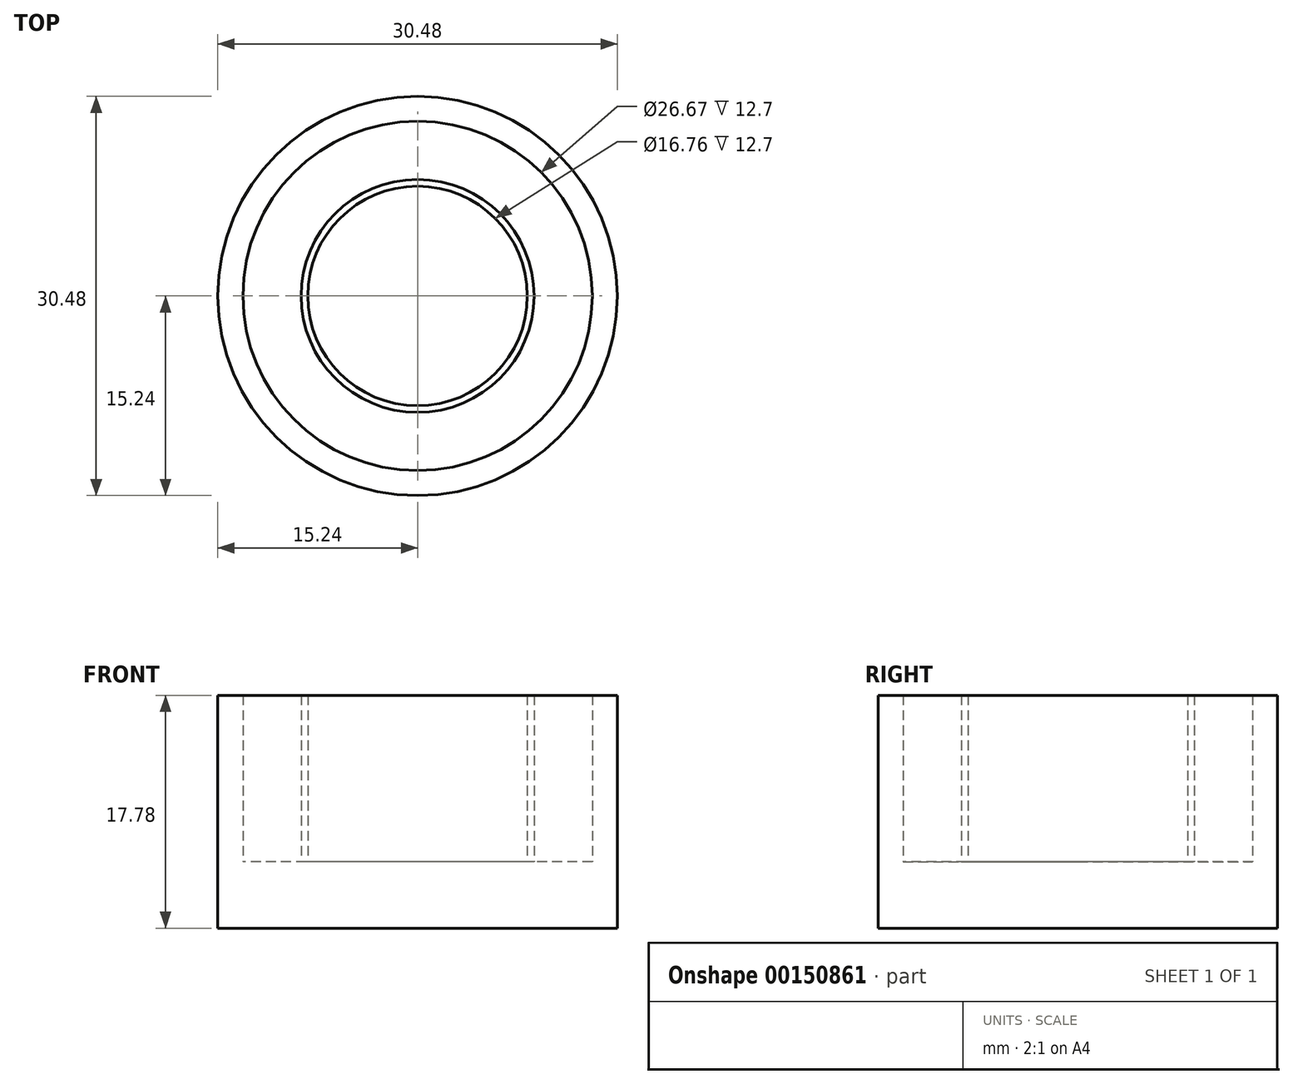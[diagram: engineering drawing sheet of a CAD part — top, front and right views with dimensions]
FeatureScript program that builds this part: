
annotation { "Feature Type Name" : "Feature", "Feature Type Description" : "" }
export const myFeature = defineFeature(function(context is Context, id is Id, definition is map)
    precondition{}
    {
        {
            var Q0;
            Q0=qCreatedBy(makeId("Top.planeOp"),FACE);
            var sketch = newSketch(context, id + "F0", { "sketchPlane" : qUnion([Q0])});
            skCircle(sketch, "E0", {"center": v(0, 0) * mm, "radius": 15.24 * mm});
            skCircle(sketch, "E1", {"center": v(0, 0) * mm, "radius": 13.34 * mm});
            skCircle(sketch, "E2", {"center": v(0, 0) * mm, "radius": 8.9 * mm});
            skCircle(sketch, "E3", {"center": v(0, 0) * mm, "radius": 8.38 * mm});
            skSolve(sketch);
        }
        {
            var Q0;
            Q0=makeQuery(id+"F0.imprint","IMPRINT",FACE,{"disambiguationData":[TD([[makeQuery(id+"F0.imprint","IMPRINT",EDGE,{"derivedFrom":sQuery(id+"F0.wireOp",EDGE,"E3")}),1.0]])]});
            var Q1;
            Q1=makeQuery(id+"F0.imprint","IMPRINT",FACE,{"disambiguationData":[TD([[makeQuery(id+"F0.imprint","IMPRINT",EDGE,{"derivedFrom":sQuery(id+"F0.wireOp",EDGE,"E0")}),1.0]])]});
            var Q2;
            Q2=makeQuery(id+"F0.imprint","IMPRINT",FACE,{"disambiguationData":[TD([[makeQuery(id+"F0.imprint","IMPRINT",EDGE,{"derivedFrom":sQuery(id+"F0.wireOp",EDGE,"E1")}),1.0]])]});
            var Q3;
            Q3=makeQuery(id+"F0.imprint","IMPRINT",FACE,{"disambiguationData":[TD([[makeQuery(id+"F0.imprint","IMPRINT",EDGE,{"derivedFrom":sQuery(id+"F0.wireOp",EDGE,"E2")}),1.0]])]});
            extrude(context, id + "F1", {"entities" : qUnion([Q0, Q1, Q2, Q3]), "depth" : 5.08 * mm});
        }
        {
            var Q0;
            Q0=makeQuery(id+"F0.imprint","IMPRINT",FACE,{"disambiguationData":[TD([[makeQuery(id+"F0.imprint","IMPRINT",EDGE,{"derivedFrom":sQuery(id+"F0.wireOp",EDGE,"E0")}),1.0]])]});
            extrude(context, id + "F2", {"entities" : qUnion([Q0]), "operationType" : NewBodyOperationType.ADD, "depth" : 17.78 * mm});
        }
        {
            var Q0;
            Q0=makeQuery(id+"F0.imprint","IMPRINT",FACE,{"disambiguationData":[TD([[makeQuery(id+"F0.imprint","IMPRINT",EDGE,{"derivedFrom":sQuery(id+"F0.wireOp",EDGE,"E2")}),1.0]])]});
            extrude(context, id + "F3", {"entities" : qUnion([Q0]), "operationType" : NewBodyOperationType.ADD, "depth" : 17.78 * mm});
        }
    });
